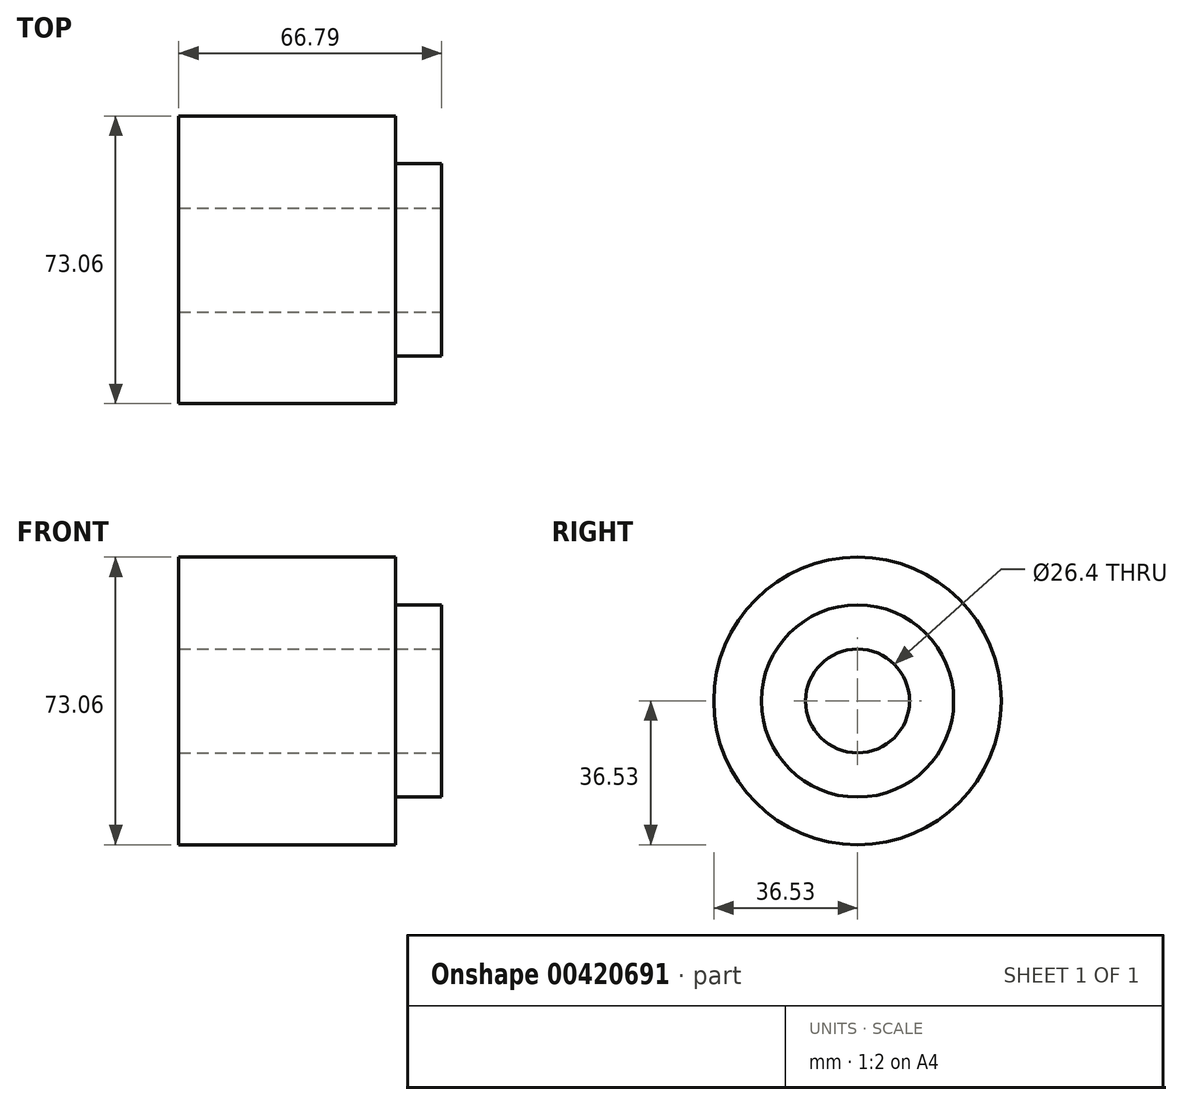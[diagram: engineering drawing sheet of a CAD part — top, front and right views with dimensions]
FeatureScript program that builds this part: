
annotation { "Feature Type Name" : "Feature", "Feature Type Description" : "" }
export const myFeature = defineFeature(function(context is Context, id is Id, definition is map)
    precondition{}
    {
        {
            var Q0;
            Q0=qCreatedBy(makeId("Front.planeOp"),FACE);
            var sketch = newSketch(context, id + "F0", { "sketchPlane" : qUnion([Q0])});
            skLineSegment(sketch, "E0", {"start": v(-180.2, 0) * mm, "end": v(95.92, 0) * mm, "construction": true});
            skLineSegment(sketch, "E1", {"start": v(0, 0) * mm, "end": v(0, 36.53) * mm});
            skLineSegment(sketch, "E2", {"start": v(0, 36.53) * mm, "end": v(55.13, 36.53) * mm});
            skLineSegment(sketch, "E3", {"start": v(55.13, 36.53) * mm, "end": v(55.13, 24.43) * mm});
            skLineSegment(sketch, "E4", {"start": v(55.13, 24.43) * mm, "end": v(66.79, 24.43) * mm});
            skLineSegment(sketch, "E5", {"start": v(66.79, 24.43) * mm, "end": v(66.79, 0) * mm});
            skLineSegment(sketch, "E6", {"start": v(66.79, 0) * mm, "end": v(0, 0) * mm});
            skSolve(sketch);
        }
        {
            var Q0;
            Q0=makeQuery(id+"F0.imprint","IMPRINT",FACE,{"disambiguationData":[TD([[makeQuery(id+"F0.imprint","IMPRINT",EDGE,{"derivedFrom":sQuery(id+"F0.wireOp",EDGE,"E1")}),-1.0]])]});
            var Q1;
            Q1=sQuery(id+"F0.wireOp",EDGE,"E0");
            revolve(context, id + "F1", {"entities" : qUnion([Q0]), "axis" : qUnion([Q1]), "revolveType" : RevolveType.FULL});
        }
        {
            var Q0;
            Q0=makeQuery(id+"F1.opRevolve","SWEPT_FACE",FACE,{"disambiguationData":[OSD([sQuery(id+"F0.wireOp",EDGE,"E5")])]});
            var sketch = newSketch(context, id + "F2", { "sketchPlane" : qUnion([Q0])});
            skSolve(sketch);
        }
        {
            var Q0;
            Q0=makeQuery(id+"F2.imprint","IMPRINT",FACE,{"disambiguationData":[TD([[makeQuery(id+"F2.imprint","IMPRINT",EDGE,{"derivedFrom":makeQuery(id+"F1.opRevolve","SWEPT_EDGE",EDGE,{"disambiguationData":[OSD([sQuery(id+"F0.wireOp",EDGE,"E4"),sQuery(id+"F0.wireOp",EDGE,"E5")])]})}),-1.0]])]});
            var sketch = newSketch(context, id + "F3", { "sketchPlane" : qUnion([Q0])});
            skCircle(sketch, "E7", {"center": v(0, 0) * mm, "radius": 13.2 * mm});
            skSolve(sketch);
        }
        {
            var Q0;
            Q0 = qSketchRegion(id + "F3", true);
            extrude(context, id + "F4", {"entities" : qUnion([Q0]), "operationType" : NewBodyOperationType.REMOVE, "endBound" : BoundingType.THROUGH_ALL, "oppositeDirection" : true, "depth" : 25.4 * mm});
        }
    });
